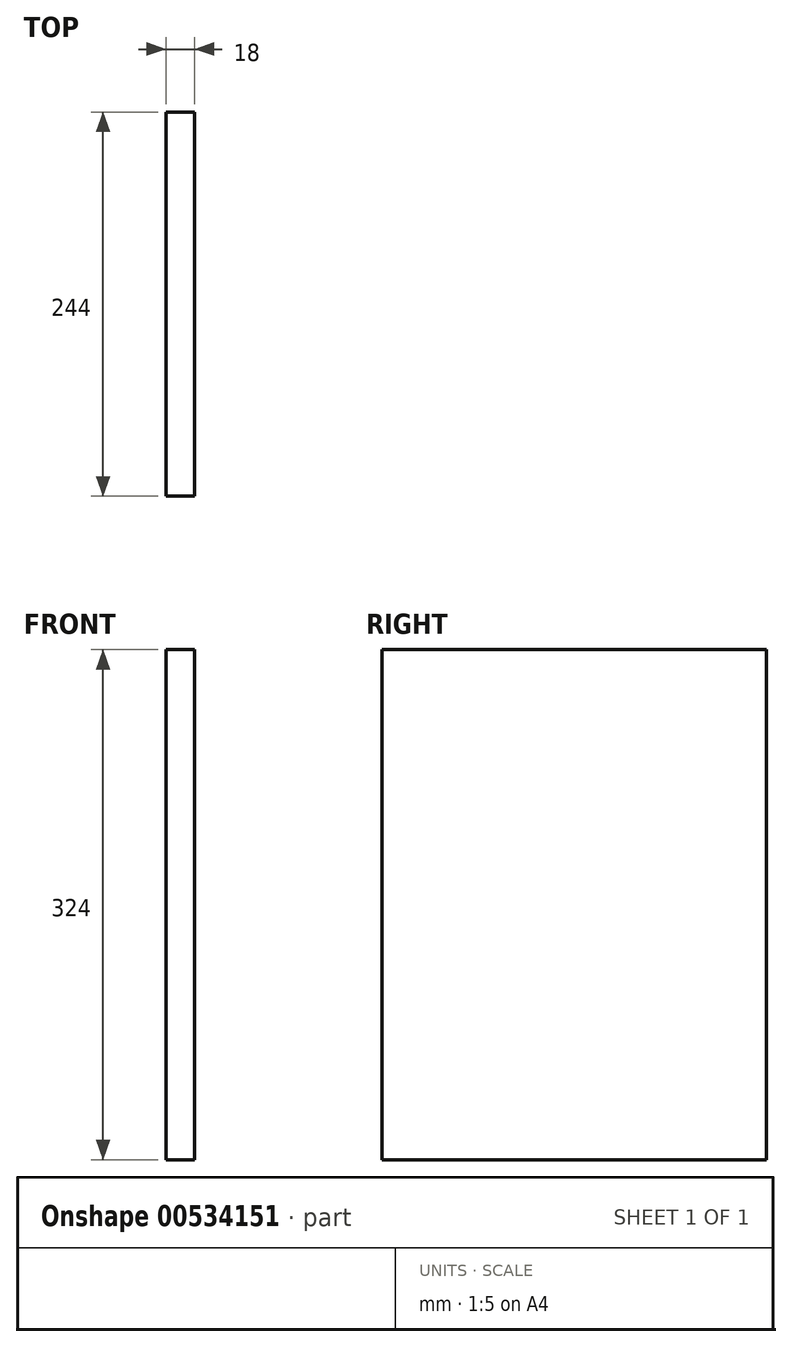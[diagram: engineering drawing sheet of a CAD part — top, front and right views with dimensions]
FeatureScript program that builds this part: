
annotation { "Feature Type Name" : "Feature", "Feature Type Description" : "" }
export const myFeature = defineFeature(function(context is Context, id is Id, definition is map)
    precondition{}
    {
        {
            var Q0;
            Q0=qCreatedBy(makeId("Right.planeOp"),FACE);
            var sketch = newSketch(context, id + "F0", { "sketchPlane" : qUnion([Q0])});
            skLineSegment(sketch, "E0.bottom", {"start": v(0, 0) * mm, "end": v(244, 0) * mm});
            skLineSegment(sketch, "E0.top", {"start": v(0, 324) * mm, "end": v(244, 324) * mm});
            skLineSegment(sketch, "E0.left", {"start": v(0, 0) * mm, "end": v(0, 324) * mm});
            skLineSegment(sketch, "E0.right", {"start": v(244, 0) * mm, "end": v(244, 324) * mm});
            skSolve(sketch);
        }
        {
            var Q0;
            Q0 = qSketchRegion(id + "F0", true);
            extrude(context, id + "F1", {"entities" : qUnion([Q0]), "depth" : 18 * mm, "offsetDistance" : 25 * mm});
        }
    });
